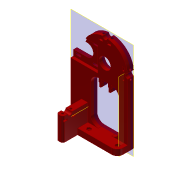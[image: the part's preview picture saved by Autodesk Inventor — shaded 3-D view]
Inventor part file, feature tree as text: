
AUTODESK INVENTOR PART (.ipt)
format: ipt  version: 2015 SP2 (Build 190223200, 223)  size: 594,432 bytes
history: native  units: mm
features: sketch x27, extrude x26, projected_geometry x11, plane x6, fillet x5, mirror x2, other x1, hole x1, chamfer x1
ambient origin geometry x8: Origin, YZ Plane, XZ Plane, XY Plane, X Axis, Y Axis, Z Axis, Center Point
bodies: Body1 (feature_tree)
feature tree (80):
  other  "Sólido1"
  extrude  "Extrusión1"  Depth=99.5mm
  extrude  "Extrusión2"  Depth=10.0mm
  extrude  "Extrusión3"  Depth=15.0mm
  fillet  "Empalme1"  Radius=49.5mm
  extrude  "Extrusión4"  Depth=154.0mm TaperAngle=0.0deg
  fillet  "Empalme2"  Radius=13.0mm
  extrude  "Extrusión6"  Depth=27.5mm
  fillet  "Empalme3"  Radius=3.0mm
  extrude  "Extrusión8"  Depth=10.0mm
  extrude  "Extrusión9"  Depth=11.0mm
  extrude  "Extrusión10"  Depth=4.0mm
  extrude  "Extrusión11"  Depth=3.5mm
  plane  "Plano de trabajo1"
  mirror  "Simetría1"
  extrude  "Extrusión12"  Depth=14.5mm
  hole  "Agujero1"  [1 undecoded]
  extrude  "Extrusión15"  Depth=20.0mm TaperAngle=0.0deg
  plane  "Plano de trabajo2"
  plane  "Plano de trabajo3"
  extrude  "Extrusión16"  Depth=10.0mm TaperAngle=0.0deg
  extrude  "Extrusión13"  Depth=6.0mm
  extrude  "Extrusión14"  Depth=2.5mm
  extrude  "Extrusión17"  Depth=5.0mm
  mirror  "Simetría2"
  extrude  "Extrusión18"  Depth=5.75mm
  extrude  "Extrusión20"  Depth=78.75mm
  extrude  "Extrusión21"  Depth=50.0mm
  extrude  "Extrusión22"  Depth=9.5mm
  extrude  "Extrusión23"  Depth=8.6mm
  sketch  "Boceto25"  dims[d64=3.5mm d65=6.0mm d66=4.0mm d67=2.0mm d68=90.0deg d69=8.0mm d70=20.594885mm d71=8.6mm]
  extrude  "Extrusión25"  Depth=8.6mm
  extrude  "Extrusión26"  Depth=6.235mm
  extrude  "Extrusión27"  Depth=3.75mm
  plane  "Plano de trabajo4"
  extrude  "Extrusión28"  Depth=14.5mm
  plane  "Plano de trabajo5"
  extrude  "Extrusión29"  Depth=0.5mm
  plane  "Plano de trabajo6"
  extrude  "Extrusión30"  Depth=0.5mm
  chamfer  "Chaflán1"  Distance=3.75mm
  fillet  "Empalme4"  Radius=3.75mm
  fillet  "Empalme5"  Radius=14.5mm
  sketch  "Boceto1"  dims[d0=29.0mm d1=99.5mm]
  sketch  "Boceto2"  dims[d2=10.0mm d3=0.0mm d4=11.0mm]
  sketch  "Boceto3"  dims[d5=144.0mm d6=0.0mm d7=15.0mm d8=49.5mm]
  sketch  "Boceto4"  dims[d9=76.5mm d10=154.0mm d11=0.0mm d12=13.0mm]
  sketch  "Boceto6"  dims[d13=22.5mm d14=27.5mm d15=3.0mm d16=0.0mm]
  sketch  "Boceto8"  dims[d20=10.0mm d21=5.0mm]
  projected_geometry  "Contorno proyectado2"
  sketch  "Boceto9"  dims[d22=40.0mm d23=11.0mm]
  projected_geometry  "Contorno proyectado3"
  sketch  "Boceto10"  dims[d24=44.0mm d25=0.0mm d26=4.0mm]
  projected_geometry  "Contorno proyectado4"
  sketch  "Boceto11"  dims[d33=3.5mm d34=3.5mm]
  sketch  "Boceto12"  dims[d35=5.25mm d36=14.5mm]
  sketch  "Boceto13"  dims[d37=20.0mm d38=0.0mm d39=8.0mm]
  sketch  "Boceto14"  dims[d40=12.5mm d41=20.0mm d42=0.0mm]
  sketch  "Boceto15"  dims[d43=10.0mm d44=20.0mm d45=0.0mm]
  sketch  "Boceto16"  dims[d46=12.5mm d47=6.0mm]
  sketch  "Boceto17"  dims[d48=2.5mm d49=2.5mm]
  projected_geometry  "Contorno proyectado5"
  sketch  "Boceto18"  dims[d50=5.0mm d51=5.0mm]
  projected_geometry  "Contorno proyectado6"
  projected_geometry  "Contorno proyectado7"
  sketch  "Boceto19"  dims[d52=21.5mm d53=5.75mm]
  sketch  "Boceto21"  dims[d54=20.0mm d55=0.0mm d57=78.75mm]
  projected_geometry  "Contorno proyectado8"
  sketch  "Boceto22"  dims[d58=20.0mm d59=0.0mm d60=50.0mm]
  sketch  "Boceto23"  dims[d61=31.5mm d62=9.5mm]
  projected_geometry  "Contorno proyectado9"
  sketch  "Boceto24"  dims[d63=20.0mm]
  projected_geometry  "Contorno proyectado10"
  projected_geometry  "Contorno proyectado11"
  sketch  "Boceto27"  dims[d72=20.0mm d73=0.0mm d74=8.6mm]
  projected_geometry  "Contorno proyectado12"
  sketch  "Boceto28"  dims[d75=20.0mm d76=0.0mm d77=6.235mm]
  sketch  "Boceto29"  dims[d78=2.79mm d79=0.0mm d80=3.75mm]
  sketch  "Boceto30"  dims[d81=3.75mm d82=14.5mm]
  sketch  "Boceto31"  dims[d86=15.0mm d87=0.0mm d88=17.5mm d89=17.5mm d90=3.75mm d91=3.75mm d92=14.5mm d93=15.0mm d94=0.0mm d95=50.0mm d96=40.0mm d97=14.0mm d98=0.0mm d101=20.6mm d102=14.0mm d103=0.0mm d104=42.5mm d105=42.5mm d106=5.0mm d107=0.0mm d108=11.0mm d109=0.0mm d110=15.0mm d111=10.0mm d112=6.0mm d113=0.0mm d114=22.3mm d127=32.65mm d129=2.1mm d130=6.0mm d131=0.0mm d132=3.8mm d133=3.8mm d134=6.0mm d135=5.7mm d136=5.7mm d137=20.0mm d139=31.0mm d140=20.0mm d142=30.1mm d145=6.0mm d146=0.0mm d147=6.0mm d148=0.0mm d149=-6.21mm d150=6.235mm d151=6.235mm d152=6.0mm d153=2.9mm d154=0.0mm d155=-6.21mm d156=6.235mm d157=6.235mm d158=6.0mm d159=2.85mm d160=0.0mm d161=-6.21mm d162=6.235mm d163=6.235mm d164=6.0mm d165=2.85mm d166=0.0mm d167=0.8mm d168=2.0mm d169=30.0deg d170=0.5mm d171=0.5mm]
note: 1 required parameter value undecoded (feature->parameter linkage not recoverable at this tier; creation-order binding heuristic only, values carry confidence <= 0.55)
